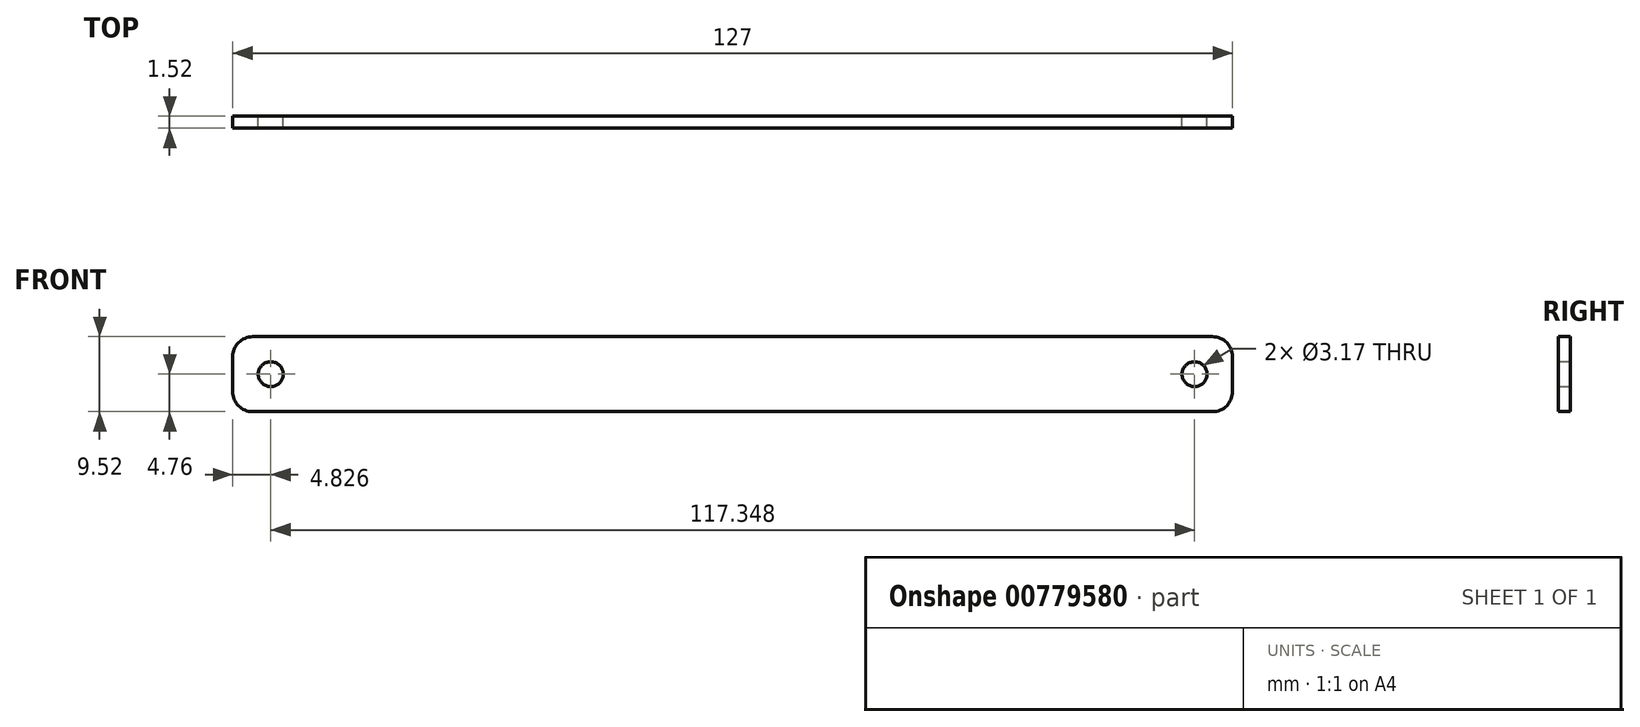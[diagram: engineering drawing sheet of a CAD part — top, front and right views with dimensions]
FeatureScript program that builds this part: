
annotation { "Feature Type Name" : "Feature", "Feature Type Description" : "" }
export const myFeature = defineFeature(function(context is Context, id is Id, definition is map)
    precondition{}
    {
        {
            var Q0;
            Q0=qCreatedBy(makeId("Front.planeOp"),FACE);
            var sketch = newSketch(context, id + "F0", { "sketchPlane" : qUnion([Q0])});
            skLineSegment(sketch, "E0.bottom", {"start": v(-63.5, 4.76) * mm, "end": v(63.5, 4.76) * mm});
            skLineSegment(sketch, "E0.top", {"start": v(-63.5, -4.76) * mm, "end": v(63.5, -4.76) * mm});
            skLineSegment(sketch, "E0.left", {"start": v(-63.5, 4.76) * mm, "end": v(-63.5, -4.76) * mm});
            skLineSegment(sketch, "E0.right", {"start": v(63.5, 4.76) * mm, "end": v(63.5, -4.76) * mm});
            skPoint(sketch, "E0.middle", {"position": v(0, 0) * mm});
            skSolve(sketch);
        }
        {
            var Q0;
            Q0=makeQuery(id+"F0.imprint","IMPRINT",FACE,{"disambiguationData":[TD([[makeQuery(id+"F0.imprint","IMPRINT",EDGE,{"derivedFrom":sQuery(id+"F0.wireOp",EDGE,"E0.bottom")}),-1.0]])]});
            extrude(context, id + "F1", {"entities" : qUnion([Q0]), "depth" : 1.52 * mm, "offsetDistance" : 25.4 * mm});
        }
        {
            var Q0;
            Q0=makeQuery(id+"F1.opExtrude","SWEPT_EDGE",EDGE,{"disambiguationData":[OSD([sQuery(id+"F0.wireOp",EDGE,"E0.bottom"),sQuery(id+"F0.wireOp",EDGE,"E0.left")])]});
            var Q1;
            Q1=makeQuery(id+"F1.opExtrude","SWEPT_EDGE",EDGE,{"disambiguationData":[OSD([sQuery(id+"F0.wireOp",EDGE,"E0.top"),sQuery(id+"F0.wireOp",EDGE,"E0.left")])]});
            var Q2;
            Q2=makeQuery(id+"F1.opExtrude","SWEPT_EDGE",EDGE,{"disambiguationData":[OSD([sQuery(id+"F0.wireOp",EDGE,"E0.top"),sQuery(id+"F0.wireOp",EDGE,"E0.right")])]});
            var Q3;
            Q3=makeQuery(id+"F1.opExtrude","SWEPT_EDGE",EDGE,{"disambiguationData":[OSD([sQuery(id+"F0.wireOp",EDGE,"E0.bottom"),sQuery(id+"F0.wireOp",EDGE,"E0.right")])]});
            fillet(context, id + "F2", {"entities" : qUnion([Q0, Q1, Q2, Q3]), "radius" : 2.54 * mm, "tangentPropagation" : true, "allowEdgeOverflow" : false});
        }
        {
            var Q0;
            Q0=makeQuery(id+"F1.opExtrude","CAP_FACE",FACE,{"disambiguationData":[OSD([sQuery(id+"F0.wireOp",EDGE,"E0.bottom"),sQuery(id+"F0.wireOp",EDGE,"E0.top"),sQuery(id+"F0.wireOp",EDGE,"E0.left"),sQuery(id+"F0.wireOp",EDGE,"E0.right")])],"isStart":false});
            var sketch = newSketch(context, id + "F3", { "sketchPlane" : qUnion([Q0])});
            skLineSegment(sketch, "E1", {"start": v(-63.5, 0) * mm, "end": v(-58.67, 0) * mm});
            skLineSegment(sketch, "E2", {"start": v(63.5, 0) * mm, "end": v(58.67, 0) * mm});
            skPoint(sketch, "E3", {"position": v(-58.67, 0) * mm});
            skPoint(sketch, "E4", {"position": v(58.67, 0) * mm});
            skSolve(sketch);
        }
        {
            var Q0;
            Q0=sQuery(id+"F3.wireOp",VERTEX,"E1.end");
            var Q1;
            Q1=sQuery(id+"F3.wireOp",VERTEX,"E4");
            var Q2;
            Q2=makeQuery(id+"F1.opExtrude","SWEPT_BODY",BODY,{"disambiguationData":[OSD([sQuery(id+"F0.wireOp",EDGE,"E0.bottom"),sQuery(id+"F0.wireOp",EDGE,"E0.top"),sQuery(id+"F0.wireOp",EDGE,"E0.left"),sQuery(id+"F0.wireOp",EDGE,"E0.right")])]});
            hole(context, id + "F4", {"style" : HoleStyle.SIMPLE, "endStyle" : HoleEndStyle.BLIND, "holeDiameter" : 3.17 * mm, "majorDiameter" : 6.35 * mm, "holeDepth" : 19.05 * mm, "isTappedThrough" : true, "tappedDepth" : 12.7 * mm, "tapClearance" : 3, "locations" : qUnion([Q0, Q1]), "scope" : qUnion([Q2]), "startStyle" : HoleStartStyle.SKETCH});
        }
    });
